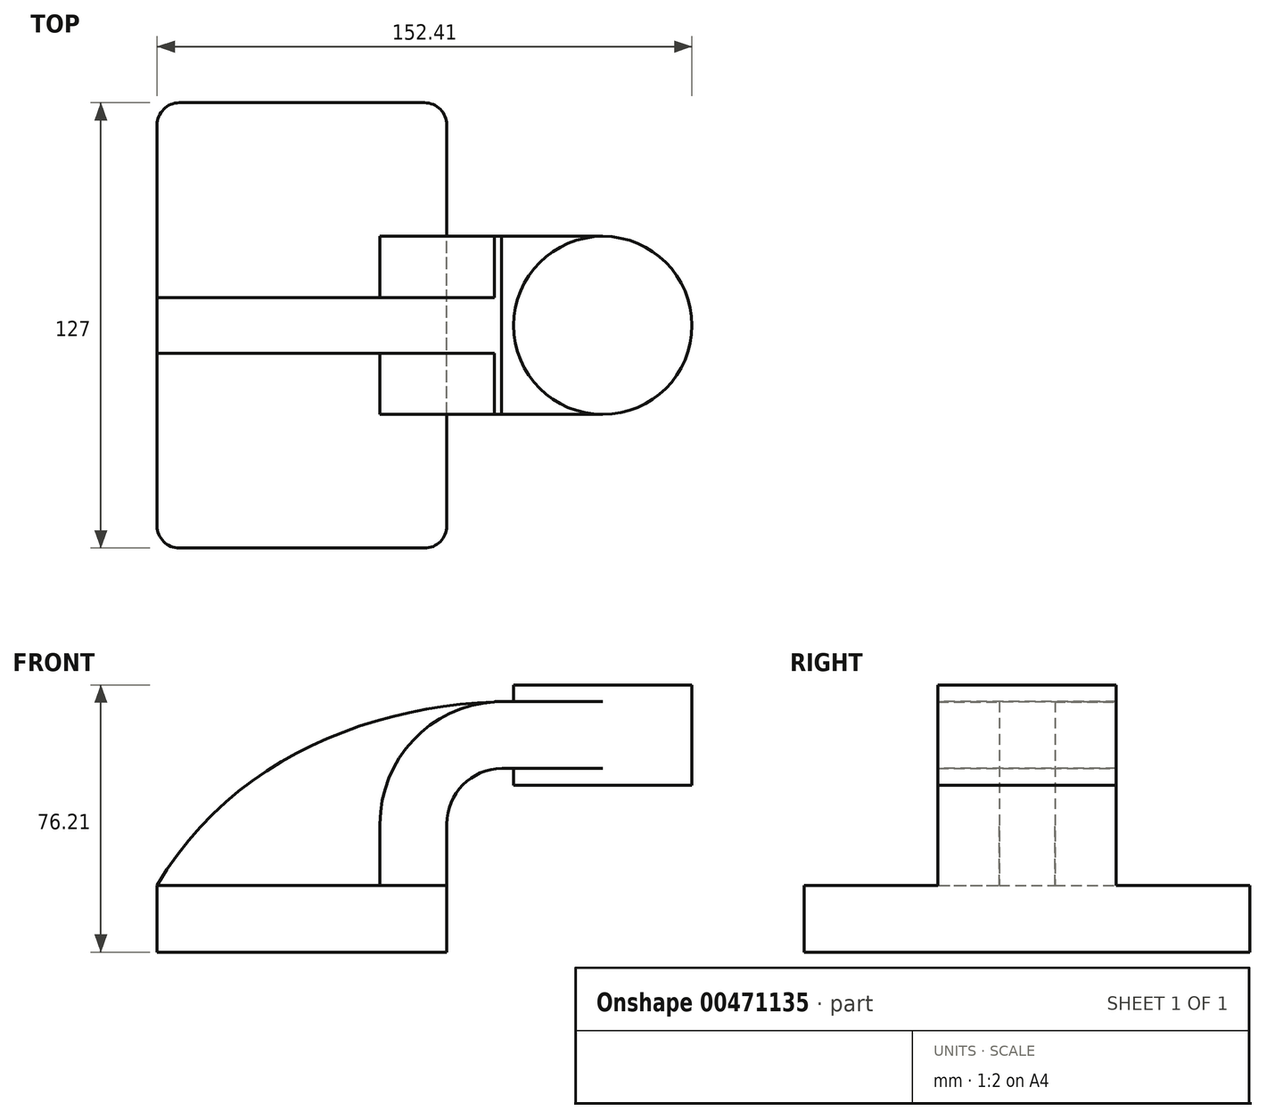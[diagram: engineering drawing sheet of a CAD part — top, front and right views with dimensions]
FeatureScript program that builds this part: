
annotation { "Feature Type Name" : "Feature", "Feature Type Description" : "" }
export const myFeature = defineFeature(function(context is Context, id is Id, definition is map)
    precondition{}
    {
        {
            var Q0;
            Q0=qCreatedBy(makeId("Front.planeOp"),FACE);
            var sketch = newSketch(context, id + "F0", { "sketchPlane" : qUnion([Q0])});
            skLineSegment(sketch, "E0.bottom", {"start": v(-41.28, 9.53) * mm, "end": v(41.28, 9.53) * mm});
            skLineSegment(sketch, "E0.top", {"start": v(-41.28, -9.52) * mm, "end": v(41.27, -9.52) * mm});
            skLineSegment(sketch, "E0.left", {"start": v(-41.28, 9.53) * mm, "end": v(-41.28, -9.52) * mm});
            skLineSegment(sketch, "E0.right", {"start": v(41.28, 9.53) * mm, "end": v(41.27, -9.52) * mm});
            skPoint(sketch, "E0.middle", {"position": v(0, 0) * mm});
            skLineSegment(sketch, "E1.bottom", {"start": v(60.32, 38.1) * mm, "end": v(111.12, 38.1) * mm});
            skLineSegment(sketch, "E1.top", {"start": v(60.33, 66.68) * mm, "end": v(111.12, 66.68) * mm});
            skLineSegment(sketch, "E1.left", {"start": v(60.32, 38.1) * mm, "end": v(60.32, 66.67) * mm});
            skLineSegment(sketch, "E1.right", {"start": v(111.12, 38.1) * mm, "end": v(111.12, 66.68) * mm});
            skPoint(sketch, "E1.middle", {"position": v(85.72, 52.39) * mm});
            skLineSegment(sketch, "E2", {"start": v(41.28, 9.53) * mm, "end": v(41.28, 27) * mm});
            skArc(sketch, "E3", {"start": v(41.27, 27) * mm, "mid": v(45.85, 38.15) * mm, "end": v(56.94, 42.88) * mm});
            skLineSegment(sketch, "E4", {"start": v(56.94, 42.88) * mm, "end": v(85.72, 42.88) * mm});
            skLineSegment(sketch, "E5.0", {"start": v(56.84, 61.93) * mm, "end": v(85.72, 61.93) * mm});
            skArc(sketch, "E5.1", {"start": v(22.22, 27) * mm, "mid": v(32.34, 51.59) * mm, "end": v(56.84, 61.93) * mm});
            skLineSegment(sketch, "E5.2", {"start": v(22.22, 9.53) * mm, "end": v(22.22, 27) * mm});
            skFitSpline(sketch, "E6", {"points": [v(56.84, 61.93) * mm, v(-41.28, 9.53) * mm], "startDerivative": vector(-114, -3.51) * mm, "endDerivative": vector(-63.51, -107.52) * mm});
            skLineSegment(sketch, "E7", {"start": v(85.72, 61.93) * mm, "end": v(85.72, 42.88) * mm});
            skLineSegment(sketch, "E8", {"start": v(85.72, 75.31) * mm, "end": v(85.72, 26.96) * mm});
            skPoint(sketch, "E8.startSnap0", {"position": v(85.72, 66.68) * mm});
            skSolve(sketch);
        }
        {
            var Q0;
            Q0=makeQuery(id+"F0.imprint","IMPRINT",FACE,{"disambiguationData":[TD([[makeQuery(id+"F0.imprint","IMPRINT",EDGE,{"derivedFrom":sQuery(id+"F0.wireOp",EDGE,"E0.top")}),1.0]])]});
            extrude(context, id + "F1", {"entities" : qUnion([Q0]), "endBound" : BoundingType.SYMMETRIC, "depth" : 127 * mm});
        }
        {
            var Q0;
            {var subQ0=sQuery(id+"F0.wireOp",EDGE,"E4");var subQ1=sQuery(id+"F0.wireOp",EDGE,"E1.left");var subQ2=makeQuery(id+"F0.imprint","INTERSECT",VERTEX,{"derivedFrom":[subQ1,subQ0]});Q0=makeQuery(id+"F0.imprint","IMPRINT",FACE,{"disambiguationData":[TD([[makeQuery(id+"F0.imprint","IMPRINT",EDGE,{"disambiguationData":[TD([[subQ2,-1.0]])],"derivedFrom":subQ1}),-1.0]])]});}
            var Q1;
            {var subQ1=sQuery(id+"F0.wireOp",EDGE,"E2");Q1=makeQuery(id+"F0.imprint","IMPRINT",FACE,{"disambiguationData":[TD([[makeQuery(id+"F0.imprint","IMPRINT",EDGE,{"derivedFrom":subQ1}),1.0]])]});}
            extrude(context, id + "F2", {"entities" : qUnion([Q0, Q1]), "operationType" : NewBodyOperationType.ADD, "endBound" : BoundingType.SYMMETRIC, "depth" : 50.8 * mm});
        }
        {
            var Q0;
            {var subQ3=sQuery(id+"F0.wireOp",EDGE,"E5.2");Q0=makeQuery(id+"F0.imprint","IMPRINT",FACE,{"disambiguationData":[TD([[makeQuery(id+"F0.imprint","IMPRINT",EDGE,{"derivedFrom":subQ3}),1.0]])]});}
            extrude(context, id + "F3", {"entities" : qUnion([Q0]), "operationType" : NewBodyOperationType.ADD, "endBound" : BoundingType.SYMMETRIC, "depth" : 15.88 * mm});
        }
        {
            var Q0;
            {var subQ4=sQuery(id+"F0.wireOp",EDGE,"E1.right");Q0=makeQuery(id+"F0.imprint","IMPRINT",FACE,{"disambiguationData":[TD([[makeQuery(id+"F0.imprint","IMPRINT",EDGE,{"derivedFrom":subQ4}),1.0]])]});}
            var Q1;
            Q1=sQuery(id+"F0.wireOp",EDGE,"E8");
            revolve(context, id + "F4", {"operationType" : NewBodyOperationType.ADD, "entities" : qUnion([Q0]), "axis" : qUnion([Q1]), "revolveType" : RevolveType.FULL});
        }
        {
            var Q0;
            Q0=makeQuery(id+"F1.opExtrude","CAP_EDGE",EDGE,{"disambiguationData":[OSD([sQuery(id+"F0.wireOp",EDGE,"E0.right")])],"isStart":false});
            var Q1;
            Q1=makeQuery(id+"F1.opExtrude","CAP_EDGE",EDGE,{"disambiguationData":[OSD([sQuery(id+"F0.wireOp",EDGE,"E0.left")])],"isStart":false});
            var Q2;
            Q2=makeQuery(id+"F1.opExtrude","CAP_EDGE",EDGE,{"disambiguationData":[OSD([sQuery(id+"F0.wireOp",EDGE,"E0.left")])],"isStart":true});
            var Q3;
            Q3=makeQuery(id+"F1.opExtrude","CAP_EDGE",EDGE,{"disambiguationData":[OSD([sQuery(id+"F0.wireOp",EDGE,"E0.right")])],"isStart":true});
            fillet(context, id + "F5", {"entities" : qUnion([Q0, Q1, Q2, Q3]), "radius" : 6.35 * mm, "tangentPropagation" : true, "allowEdgeOverflow" : false});
        }
    });
